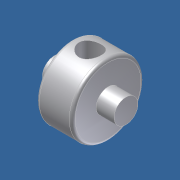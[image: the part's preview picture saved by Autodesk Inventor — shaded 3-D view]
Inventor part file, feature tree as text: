
AUTODESK INVENTOR PART (.ipt)
format: ipt  version: unknown  size: 207,872 bytes
history: native  units: in
note: dims shown in document units (in); Inventor stores cm internally (conversion verified against a paired STEP export)
features: sketch x2, revolve x1, fillet x1, plane x1, hole x1
ambient origin geometry x8: Origin, YZ Plane, XZ Plane, XY Plane, X Axis, Y Axis, Z Axis, Center Point
bodies: Solid1 (feature_tree)
feature tree (6):
  revolve  "Revolution1"  [1 undecoded]
  fillet  "Fillet1"  Radius=0.75in
  plane  "Work Plane1"
  hole  "Hole1"  [1 undecoded]
  sketch  "Sketch1"  dims[d0=0.1875in d1=0.1875in d2=0.75in]
  sketch  "Sketch2"  dims[d3=0.125in d4=0.125in d5=0.375in d6=90.0deg d7=0.0312in d8=0.2343in d9=0.75in d10=0.375in d11=0.25in d12=0.5635in d13=1.0in d14=0.8108in]
note: 2 required parameter values undecoded (feature->parameter linkage not recoverable at this tier; creation-order binding heuristic only, values carry confidence <= 0.55)